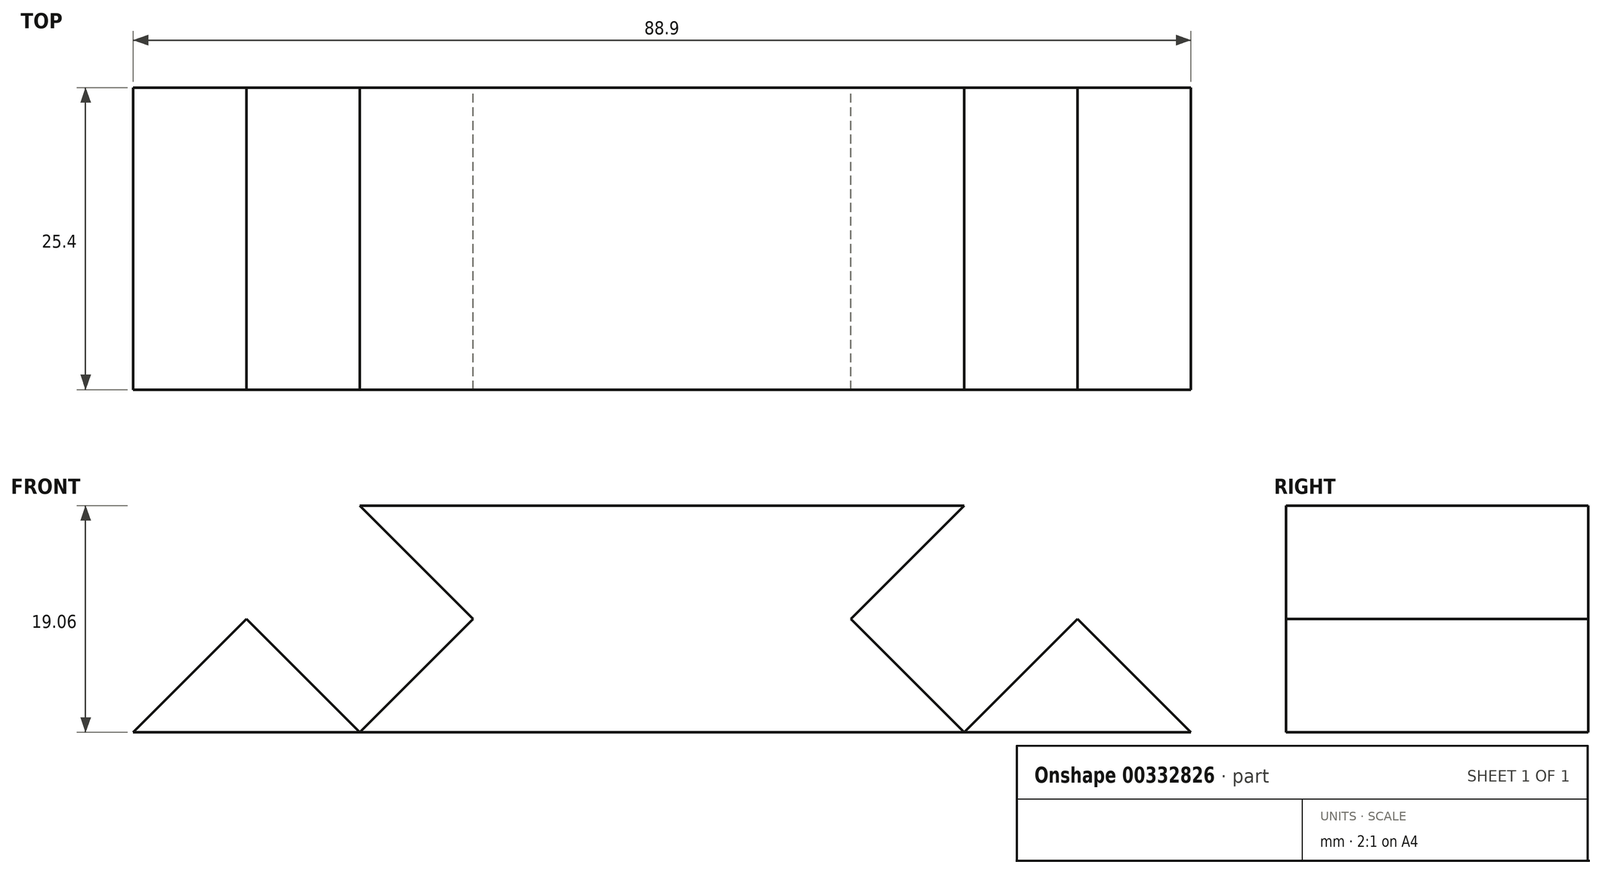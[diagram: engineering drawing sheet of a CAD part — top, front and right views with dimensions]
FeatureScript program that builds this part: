
annotation { "Feature Type Name" : "Feature", "Feature Type Description" : "" }
export const myFeature = defineFeature(function(context is Context, id is Id, definition is map)
    precondition{}
    {
        {
            var Q0;
            Q0=qCreatedBy(makeId("Front.planeOp"),FACE);
            var sketch = newSketch(context, id + "F0", { "sketchPlane" : qUnion([Q0])});
            skLineSegment(sketch, "E0.bottom", {"start": v(-25.4, -9.53) * mm, "end": v(25.4, -9.53) * mm});
            skLineSegment(sketch, "E0.top", {"start": v(-25.4, 9.52) * mm, "end": v(25.4, 9.52) * mm});
            skPoint(sketch, "E0.middle", {"position": v(0, 0) * mm});
            skLineSegment(sketch, "E1", {"start": v(25.4, -9.53) * mm, "end": v(15.88, 0) * mm});
            skLineSegment(sketch, "E2", {"start": v(25.4, 9.53) * mm, "end": v(15.88, 0) * mm});
            skLineSegment(sketch, "E3", {"start": v(25.4, -9.53) * mm, "end": v(34.92, 0) * mm});
            skLineSegment(sketch, "E4", {"start": v(25.4, -9.53) * mm, "end": v(44.45, -9.53) * mm});
            skLineSegment(sketch, "E5", {"start": v(34.92, 0) * mm, "end": v(44.45, -9.53) * mm});
            skLineSegment(sketch, "E6.MirrorCS", {"start": v(-25.4, -9.52) * mm, "end": v(-34.92, 0) * mm});
            skLineSegment(sketch, "E7.MirrorCS", {"start": v(25.4, -9.53) * mm, "end": v(-25.4, -9.53) * mm});
            skLineSegment(sketch, "E8.MirrorCS", {"start": v(25.4, 9.52) * mm, "end": v(-25.4, 9.52) * mm});
            skLineSegment(sketch, "E9.MirrorCS", {"start": v(-25.4, -9.53) * mm, "end": v(-15.88, 0) * mm});
            skLineSegment(sketch, "E10.MirrorCS", {"start": v(-25.4, -9.53) * mm, "end": v(-44.45, -9.53) * mm});
            skLineSegment(sketch, "E11.MirrorCS", {"start": v(-25.4, 9.53) * mm, "end": v(-15.88, 0) * mm});
            skLineSegment(sketch, "E12.MirrorCS", {"start": v(-34.92, 0) * mm, "end": v(-44.45, -9.53) * mm});
            skPoint(sketch, "E13.orphan", {"position": v(-29.9, 9.52) * mm});
            skSolve(sketch);
        }
        {
            var Q0;
            Q0 = qSketchRegion(id + "F0", true);
            extrude(context, id + "F1", {"entities" : qUnion([Q0]), "depth" : 25.4 * mm});
        }
    });
